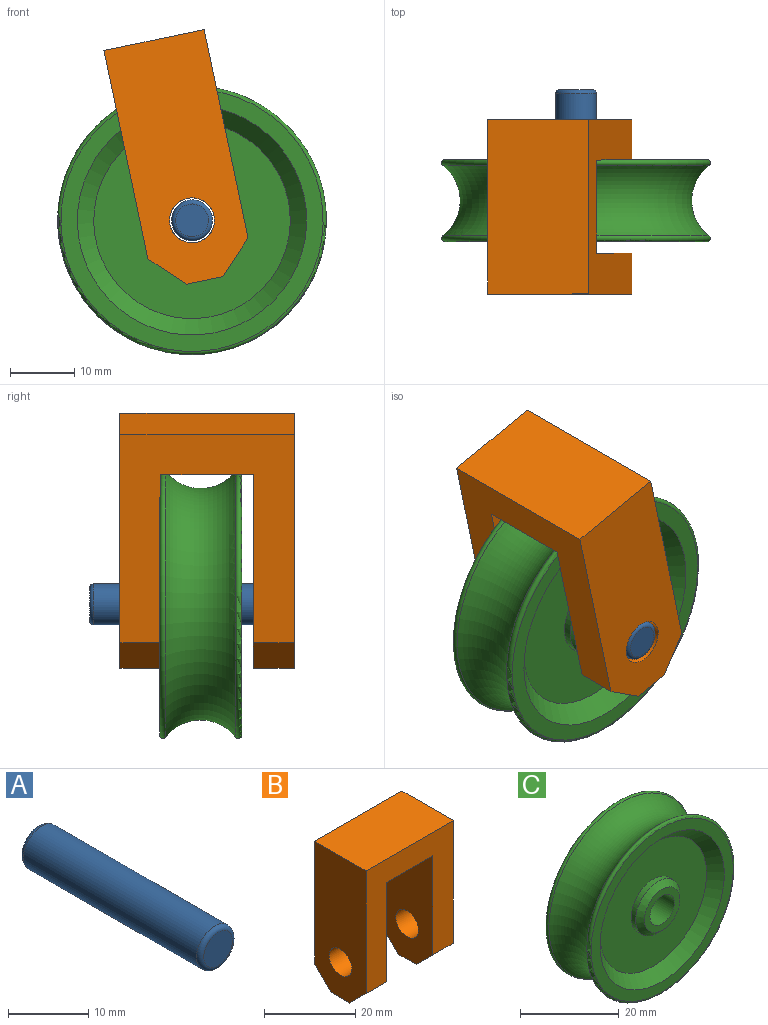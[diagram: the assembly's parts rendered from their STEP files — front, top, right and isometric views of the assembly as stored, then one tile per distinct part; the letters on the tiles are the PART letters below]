
ASSEMBLY  parts=3 mates=3
PART A: 5 faces, bbox 6.9x31.8x6.9 mm
  f0: cylinder r=3.17mm len=30.48mm, axis (0,1,0), area 608mm2, adj f3,f4
  f1: plane 5.08x5.08mm, normal (0,-1,0), area 20.3mm2, adj f4
  f2: plane 5.08x5.08mm, normal (0,1,0), area 20.3mm2, adj f3
  f3: torus R=2.54mm, axis (0,-1,0), area 18.5mm2, adj f0,f2
  f4: torus R=2.54mm, axis (0,-1,0), area 18.5mm2, adj f0,f1
PART B: 16 faces, bbox 27.1x15.9x38.1 mm
  f0: plane 15.88x14.35mm, normal (0,0,-1), area 227.8mm2, adj f2,f4,f7,f8
  f1: plane 38.1x15.88mm, normal (-1,0,0), area 540.7mm2, adj f2,f4,f5,f9,f11,f13,f14
  f2: plane 33.02x27.05mm, normal (0,-1,0), area 510.5mm2, adj f0,f1,f3,f5,f7,f8,f12,f13
  f3: plane 38.1x15.88mm, normal (1,0,0), area 540.7mm2, adj f2,f4,f5,f6,f10,f12,f15
  f4: plane 33.02x27.05mm, normal (0,1,0), area 510.5mm2, adj f0,f1,f3,f5,f7,f8,f10,f11
  f5: plane 27.05x15.88mm, normal (0,0,1), area 429.4mm2, adj f1,f2,f3,f4
  f6: plane 6.35x5.72mm, normal (0,0,-1), area 36.3mm2, adj f3,f7,f10,f12
  f7: plane 31.75x15.88mm, normal (-1,0,0), area 439.9mm2, adj f0,f2,f4,f6,f10,f12,f15
  f8: plane 31.75x15.88mm, normal (1,0,0), area 439.9mm2, adj f0,f2,f4,f9,f11,f13,f14
  f9: plane 6.35x5.72mm, normal (0,0,-1), area 36.3mm2, adj f1,f8,f11,f13
  f10: plane 6.35x5.08mm, normal (0,0.71,-0.71), area 45.6mm2, adj f3,f4,f6,f7
  f11: plane 6.35x5.08mm, normal (0,0.71,-0.71), area 45.6mm2, adj f1,f4,f8,f9
  f12: plane 6.35x5.08mm, normal (0,-0.71,-0.71), area 45.6mm2, adj f2,f3,f6,f7
  f13: plane 6.35x5.08mm, normal (0,-0.71,-0.71), area 45.6mm2, adj f1,f2,f8,f9
  f14: cylinder r=3.49mm len=6.99mm, axis (-1,0,0), area 139.3mm2, adj f1,f8
  f15: cylinder r=3.49mm len=6.99mm, axis (-1,0,0), area 139.3mm2, adj f3,f7
PART C: 16 faces, bbox 53.7x13.7x53.7 mm
  f0: plane 40.67x40.67mm, normal (0,-1,0), area 305.8mm2, adj f3,f8
  f1: torus R=24.83mm, axis (0,-1,0), area 1490.2mm2, adj f3,f4
  f2: plane 40.67x40.67mm, normal (0,1,0), area 305.8mm2, adj f4,f6
  f3: torus R=20.33mm, axis (0,1,0), area 164.2mm2, adj f0,f1
  f4: torus R=20.33mm, axis (0,1,0), area 164.2mm2, adj f1,f2
  f5: plane 30.48x30.48mm, normal (0,1,0), area 603mm2, adj f6,f9
  f6: cone r=12.7mm half-angle=45deg, axis (0,1,0), area 372.6mm2, adj f2,f5
  f7: plane 30.48x30.48mm, normal (0,-1,0), area 603mm2, adj f8,f12
  f8: cone r=12.7mm half-angle=45deg, axis (0,-1,0), area 372.6mm2, adj f0,f7
  f9: cylinder r=6.35mm len=12.7mm, axis (0,-1,0), area 50.7mm2, adj f5,f11
  f10: plane 10.16x10.16mm, normal (0,1,0), area 42.8mm2, adj f11,f14
  f11: cone r=5.08mm half-angle=45deg, axis (0,-1,0), area 64.5mm2, adj f9,f10
  f12: cylinder r=6.35mm len=12.7mm, axis (0,1,0), area 50.7mm2, adj f7,f15
  f13: plane 10.16x10.16mm, normal (0,-1,0), area 42.8mm2, adj f14,f15
  f14: cylinder r=3.49mm len=12.7mm, axis (0,-1,0), area 278.7mm2, adj f10,f13
  f15: cone r=5.08mm half-angle=45deg, axis (0,1,0), area 64.5mm2, adj f12,f13
PLACE A rot(axis=(0,-1,0),3.5deg) t=(-88.77,-52.1,-26.59)mm
PLACE B rot(axis=(-0.1,-0.1,0.99),90.6deg) t=(-85.59,-83.85,-3.2)mm
PLACE C rot(axis=(0,-1,0),3.5deg) t=(-88.77,-62.97,-26.59)mm
MATE planar A.f0 <-> B.f1  axis (0,-1,0) through (-88.77,-83.85,-26.59)mm
MATE cylindrical A.f0 <-> C.f14  axis (0,1,0) through (-88.77,-67.97,-26.59)mm
MATE cylindrical A.f0 <-> B.f14  axis (0,1,0) through (-88.77,-52.73,-26.59)mm
